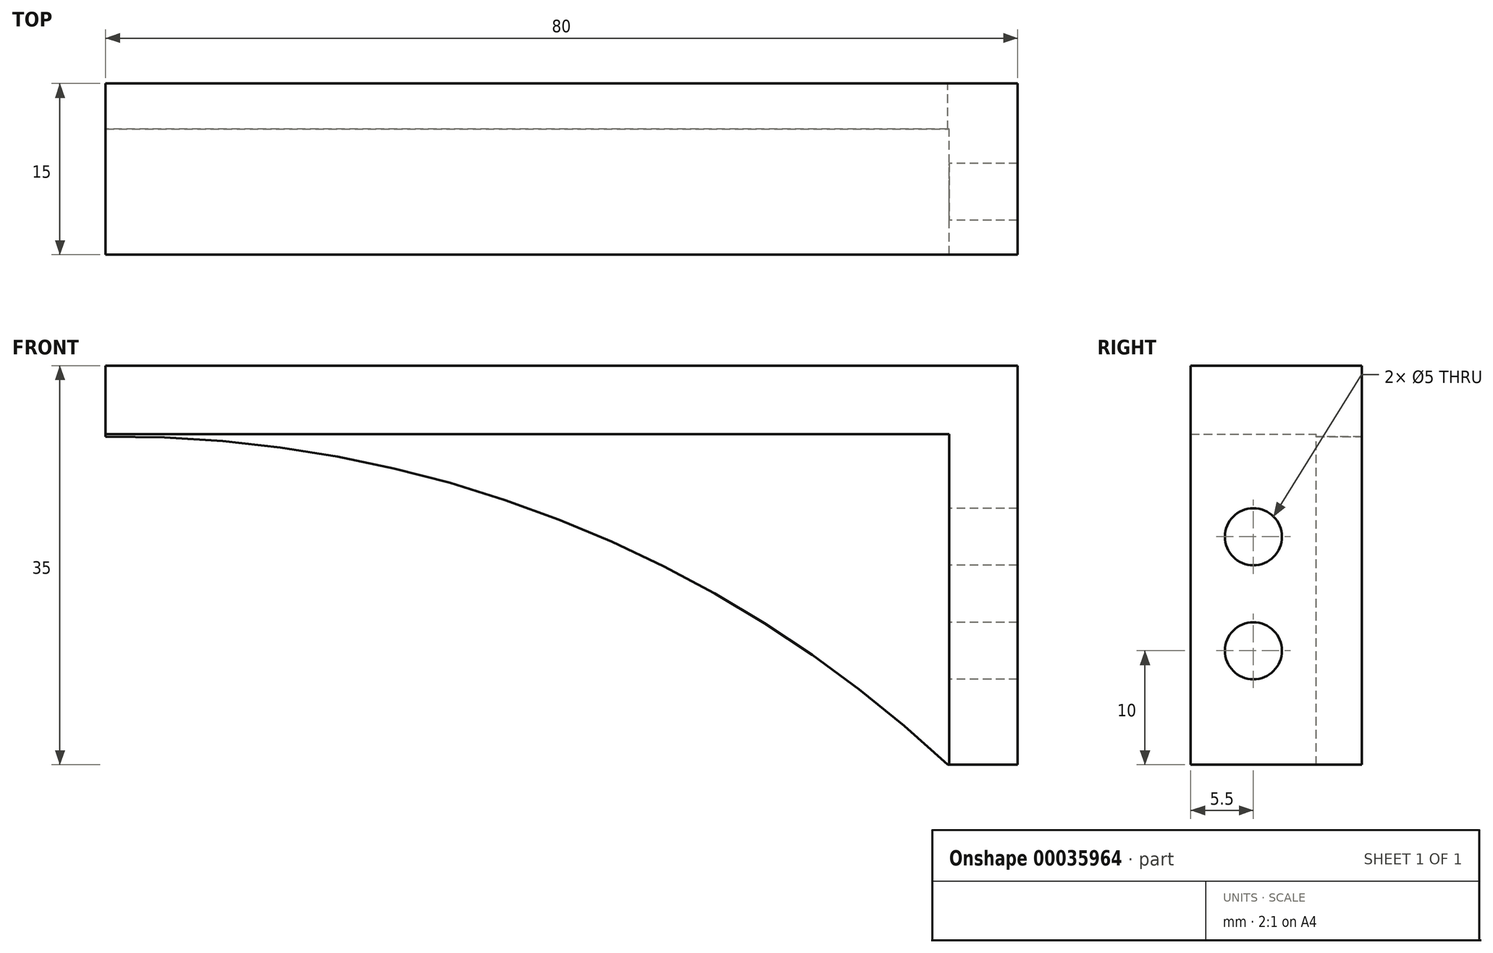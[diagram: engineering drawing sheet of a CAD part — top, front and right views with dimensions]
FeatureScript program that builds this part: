
annotation { "Feature Type Name" : "Feature", "Feature Type Description" : "" }
export const myFeature = defineFeature(function(context is Context, id is Id, definition is map)
    precondition{}
    {
        {
            var Q0;
            Q0=qCreatedBy(makeId("Front.planeOp"),FACE);
            var sketch = newSketch(context, id + "F0", { "sketchPlane" : qUnion([Q0])});
            skLineSegment(sketch, "E0.bottom", {"start": v(0, 0) * mm, "end": v(-80, 0) * mm});
            skLineSegment(sketch, "E0.top", {"start": v(0, 35) * mm, "end": v(-80, 35) * mm});
            skLineSegment(sketch, "E0.left", {"start": v(0, 0) * mm, "end": v(0, 35) * mm});
            skLineSegment(sketch, "E0.right", {"start": v(-80, 0) * mm, "end": v(-80, 35) * mm});
            skSolve(sketch);
        }
        {
            var Q0;
            Q0=makeQuery(id+"F0.imprint","IMPRINT",FACE,{"disambiguationData":[TD([[makeQuery(id+"F0.imprint","IMPRINT",EDGE,{"derivedFrom":sQuery(id+"F0.wireOp",EDGE,"E0.bottom")}),-1.0]])]});
            extrude(context, id + "F1", {"entities" : qUnion([Q0]), "depth" : 15 * mm});
        }
        {
            var Q0;
            Q0=qCreatedBy(makeId("Front.planeOp"),FACE);
            var sketch = newSketch(context, id + "F2", { "sketchPlane" : qUnion([Q0])});
            skLineSegment(sketch, "E1.bottom", {"start": v(-86, -11) * mm, "end": v(-6, -11) * mm});
            skLineSegment(sketch, "E1.top", {"start": v(-86, 29) * mm, "end": v(-6, 29) * mm});
            skLineSegment(sketch, "E1.left", {"start": v(-86, -11) * mm, "end": v(-86, 29) * mm});
            skLineSegment(sketch, "E1.right", {"start": v(-6, -11) * mm, "end": v(-6, 29) * mm});
            skSolve(sketch);
        }
        {
            var Q0;
            Q0=makeQuery(id+"F2.imprint","IMPRINT",FACE,{"disambiguationData":[TD([[makeQuery(id+"F2.imprint","IMPRINT",EDGE,{"derivedFrom":sQuery(id+"F2.wireOp",EDGE,"E1.bottom")}),1.0]])]});
            extrude(context, id + "F3", {"entities" : qUnion([Q0]), "operationType" : NewBodyOperationType.REMOVE, "depth" : 25 * mm, "hasSecondDirection" : true, "secondDirectionOppositeDirection" : false, "secondDirectionDepth" : 4 * mm});
        }
        {
            var Q0;
            Q0=qCreatedBy(makeId("Front.planeOp"),FACE);
            var sketch = newSketch(context, id + "F4", { "sketchPlane" : qUnion([Q0])});
            skArc(sketch, "E2", {"start": v(-6.12, 0) * mm, "mid": v(-40.27, 21.52) * mm, "end": v(-79.96, 28.78) * mm});
            skLineSegment(sketch, "E3", {"start": v(-79.96, 28.78) * mm, "end": v(-95.13, 28.63) * mm});
            skLineSegment(sketch, "E4", {"start": v(-95.13, 28.63) * mm, "end": v(-94.73, -12.51) * mm});
            skLineSegment(sketch, "E5", {"start": v(-94.73, -12.51) * mm, "end": v(-6.12, -12.51) * mm});
            skLineSegment(sketch, "E6", {"start": v(-6.12, -12.51) * mm, "end": v(-6.12, 0) * mm});
            skSolve(sketch);
        }
        {
            var Q0;
            Q0=makeQuery(id+"F4.imprint","IMPRINT",FACE,{"disambiguationData":[TD([[makeQuery(id+"F4.imprint","IMPRINT",EDGE,{"derivedFrom":sQuery(id+"F4.wireOp",EDGE,"E2")}),1.0]])]});
            extrude(context, id + "F5", {"entities" : qUnion([Q0]), "operationType" : NewBodyOperationType.REMOVE, "depth" : 25 * mm, "hasSecondDirection" : true, "secondDirectionOppositeDirection" : true, "secondDirectionDepth" : 25 * mm});
        }
        {
            var Q0;
            Q0=qCreatedBy(makeId("Right.planeOp"),FACE);
            var sketch = newSketch(context, id + "F6", { "sketchPlane" : qUnion([Q0])});
            skLineSegment(sketch, "E7", {"start": v(0, 0) * mm, "end": v(-9.5, 0) * mm});
            skLineSegment(sketch, "E8", {"start": v(-9.5, 0) * mm, "end": v(-9.5, 7.5) * mm});
            skCircle(sketch, "E9", {"center": v(-9.5, 20) * mm, "radius": 2.5 * mm});
            skCircle(sketch, "E10", {"center": v(-9.5, 10) * mm, "radius": 2.5 * mm});
            skSolve(sketch);
        }
        {
            var Q0;
            Q0 = qSketchRegion(id + "F6", true);
            extrude(context, id + "F7", {"entities" : qUnion([Q0]), "operationType" : NewBodyOperationType.REMOVE, "depth" : 25 * mm, "hasSecondDirection" : true, "secondDirectionOppositeDirection" : true, "secondDirectionDepth" : 25 * mm});
        }
    });
